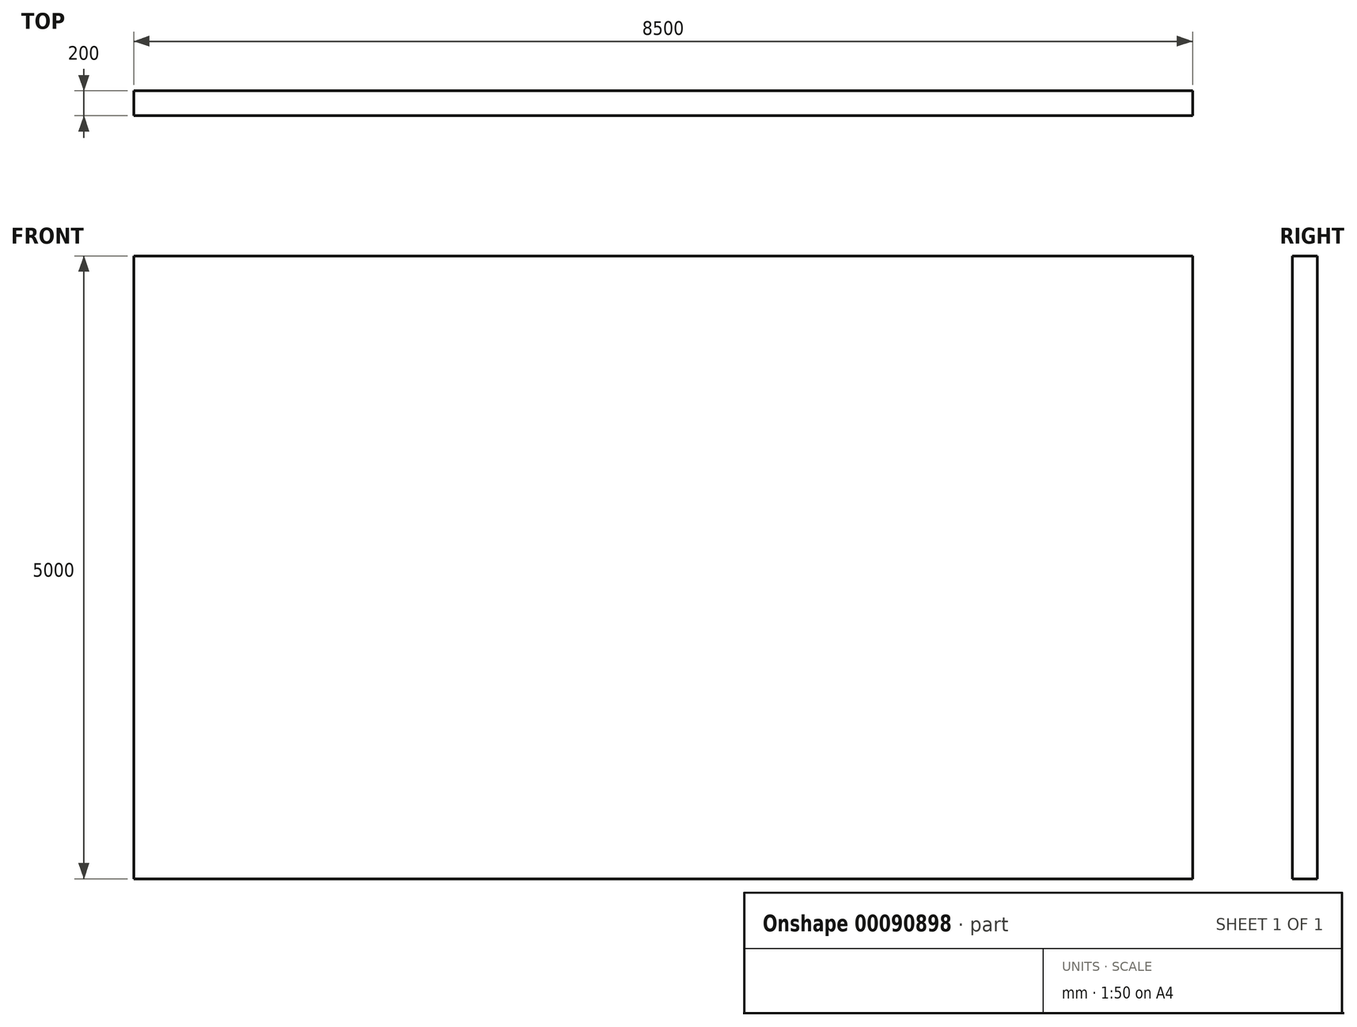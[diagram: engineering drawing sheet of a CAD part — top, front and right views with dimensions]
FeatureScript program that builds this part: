
annotation { "Feature Type Name" : "Feature", "Feature Type Description" : "" }
export const myFeature = defineFeature(function(context is Context, id is Id, definition is map)
    precondition{}
    {
        {
            var Q0;
            Q0=qCreatedBy(makeId("Front.planeOp"),FACE);
            var sketch = newSketch(context, id + "F0", { "sketchPlane" : qUnion([Q0])});
            skLineSegment(sketch, "E0.bottom", {"start": v(-3762.35, 3430.5) * mm, "end": v(4737.65, 3430.5) * mm});
            skLineSegment(sketch, "E0.top", {"start": v(-3762.35, -1569.5) * mm, "end": v(4737.65, -1569.5) * mm});
            skLineSegment(sketch, "E0.left", {"start": v(-3762.35, 3430.5) * mm, "end": v(-3762.35, -1569.5) * mm});
            skLineSegment(sketch, "E0.right", {"start": v(4737.65, 3430.5) * mm, "end": v(4737.65, -1569.5) * mm});
            skSolve(sketch);
        }
        {
            var Q0;
            Q0 = qSketchRegion(id + "F0", true);
            extrude(context, id + "F1", {"entities" : qUnion([Q0]), "depth" : 200 * mm});
        }
    });
